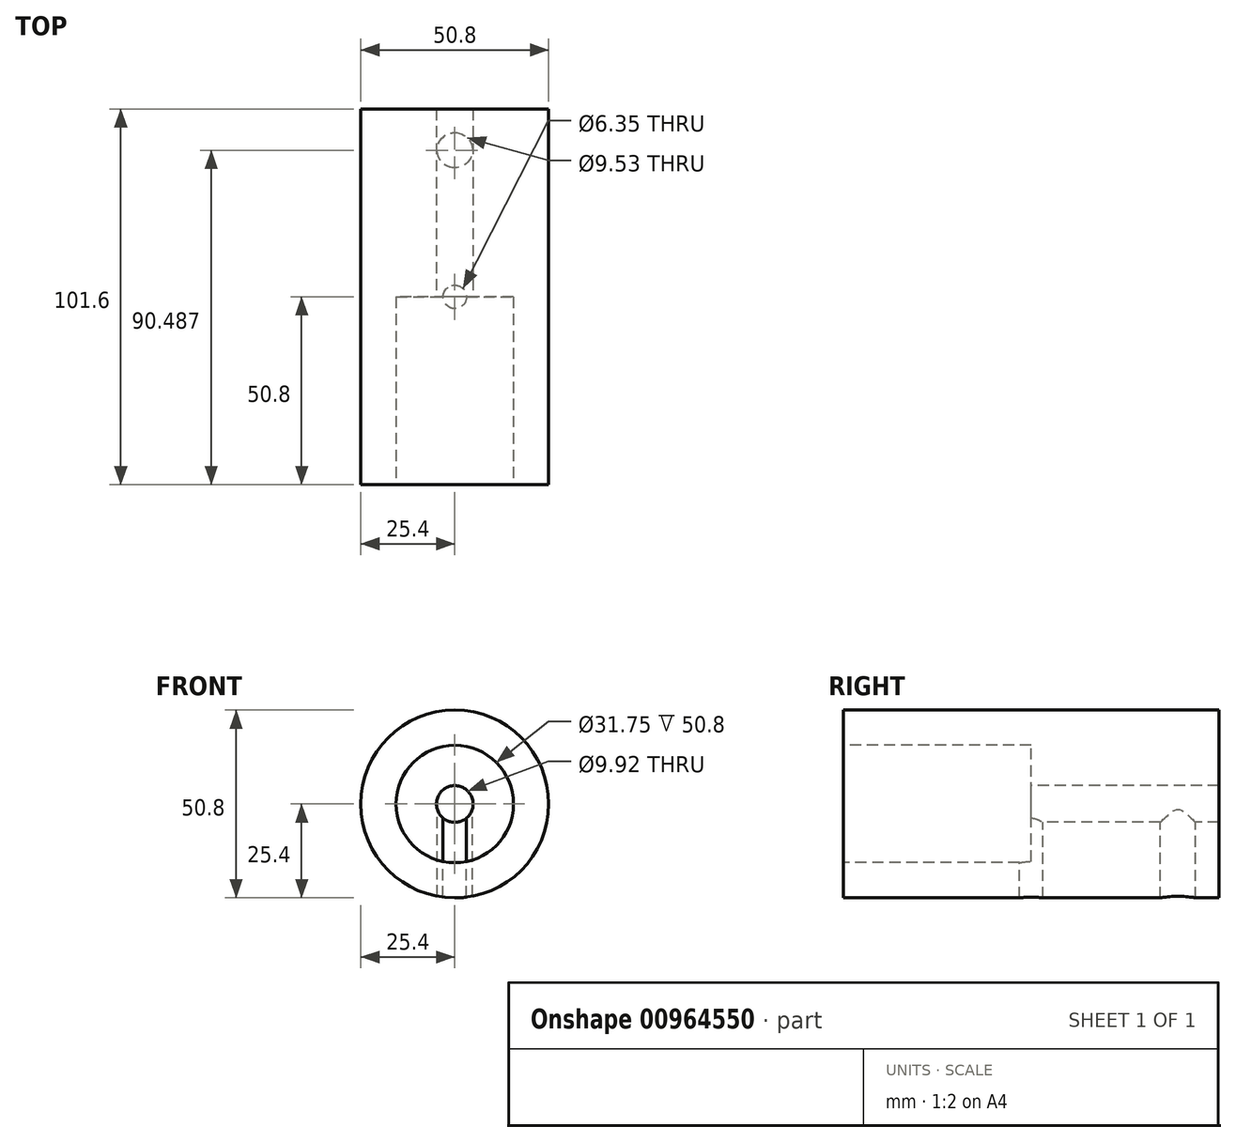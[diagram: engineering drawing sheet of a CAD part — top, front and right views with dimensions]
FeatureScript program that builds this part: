
annotation { "Feature Type Name" : "Feature", "Feature Type Description" : "" }
export const myFeature = defineFeature(function(context is Context, id is Id, definition is map)
    precondition{}
    {
        {
            var Q0;
            Q0=qCreatedBy(makeId("Front.planeOp"),FACE);
            var sketch = newSketch(context, id + "F0", { "sketchPlane" : qUnion([Q0])});
            skCircle(sketch, "E0", {"center": v(0, 0) * mm, "radius": 25.4 * mm});
            skSolve(sketch);
        }
        {
            var Q0;
            Q0 = qSketchRegion(id + "F0", true);
            extrude(context, id + "F1", {"entities" : qUnion([Q0]), "oppositeDirection" : true, "depth" : 101.6 * mm, "offsetDistance" : 25.4 * mm});
        }
        {
            var Q0;
            Q0=qCreatedBy(makeId("Front.planeOp"),FACE);
            var sketch = newSketch(context, id + "F2", { "sketchPlane" : qUnion([Q0])});
            skCircle(sketch, "E1", {"center": v(0, 0) * mm, "radius": 15.88 * mm});
            skSolve(sketch);
        }
        {
            var Q0;
            Q0 = qSketchRegion(id + "F2", true);
            extrude(context, id + "F3", {"entities" : qUnion([Q0]), "operationType" : NewBodyOperationType.REMOVE, "oppositeDirection" : true, "depth" : 50.8 * mm, "offsetDistance" : 25.4 * mm});
        }
        {
            var Q0;
            Q0=qCreatedBy(makeId("Front.planeOp"),FACE);
            var sketch = newSketch(context, id + "F4", { "sketchPlane" : qUnion([Q0])});
            skCircle(sketch, "E2", {"center": v(0, 0) * mm, "radius": 4.96 * mm});
            skSolve(sketch);
        }
        {
            var Q0;
            Q0 = qSketchRegion(id + "F4", true);
            extrude(context, id + "F5", {"entities" : qUnion([Q0]), "operationType" : NewBodyOperationType.REMOVE, "endBound" : BoundingType.THROUGH_ALL, "oppositeDirection" : true, "depth" : 25.4 * mm, "offsetDistance" : 25.4 * mm});
        }
        {
            var Q0;
            Q0=qCreatedBy(makeId("Top.planeOp"),FACE);
            var sketch = newSketch(context, id + "F6", { "sketchPlane" : qUnion([Q0])});
            skCircle(sketch, "E3", {"center": v(0, 50.8) * mm, "radius": 3.18 * mm});
            skSolve(sketch);
        }
        {
            var Q0;
            Q0 = qSketchRegion(id + "F6", true);
            extrude(context, id + "F7", {"entities" : qUnion([Q0]), "operationType" : NewBodyOperationType.REMOVE, "oppositeDirection" : true, "depth" : 25.4 * mm, "offsetDistance" : 25.4 * mm});
        }
        {
            var Q0;
            Q0=qCreatedBy(makeId("Top.planeOp"),FACE);
            var sketch = newSketch(context, id + "F8", { "sketchPlane" : qUnion([Q0])});
            skCircle(sketch, "E4", {"center": v(0, 90.49) * mm, "radius": 4.76 * mm});
            skSolve(sketch);
        }
        {
            var Q0;
            Q0 = qSketchRegion(id + "F8", true);
            extrude(context, id + "F9", {"entities" : qUnion([Q0]), "operationType" : NewBodyOperationType.REMOVE, "oppositeDirection" : true, "depth" : 127 * mm, "offsetDistance" : 25.4 * mm});
        }
    });
